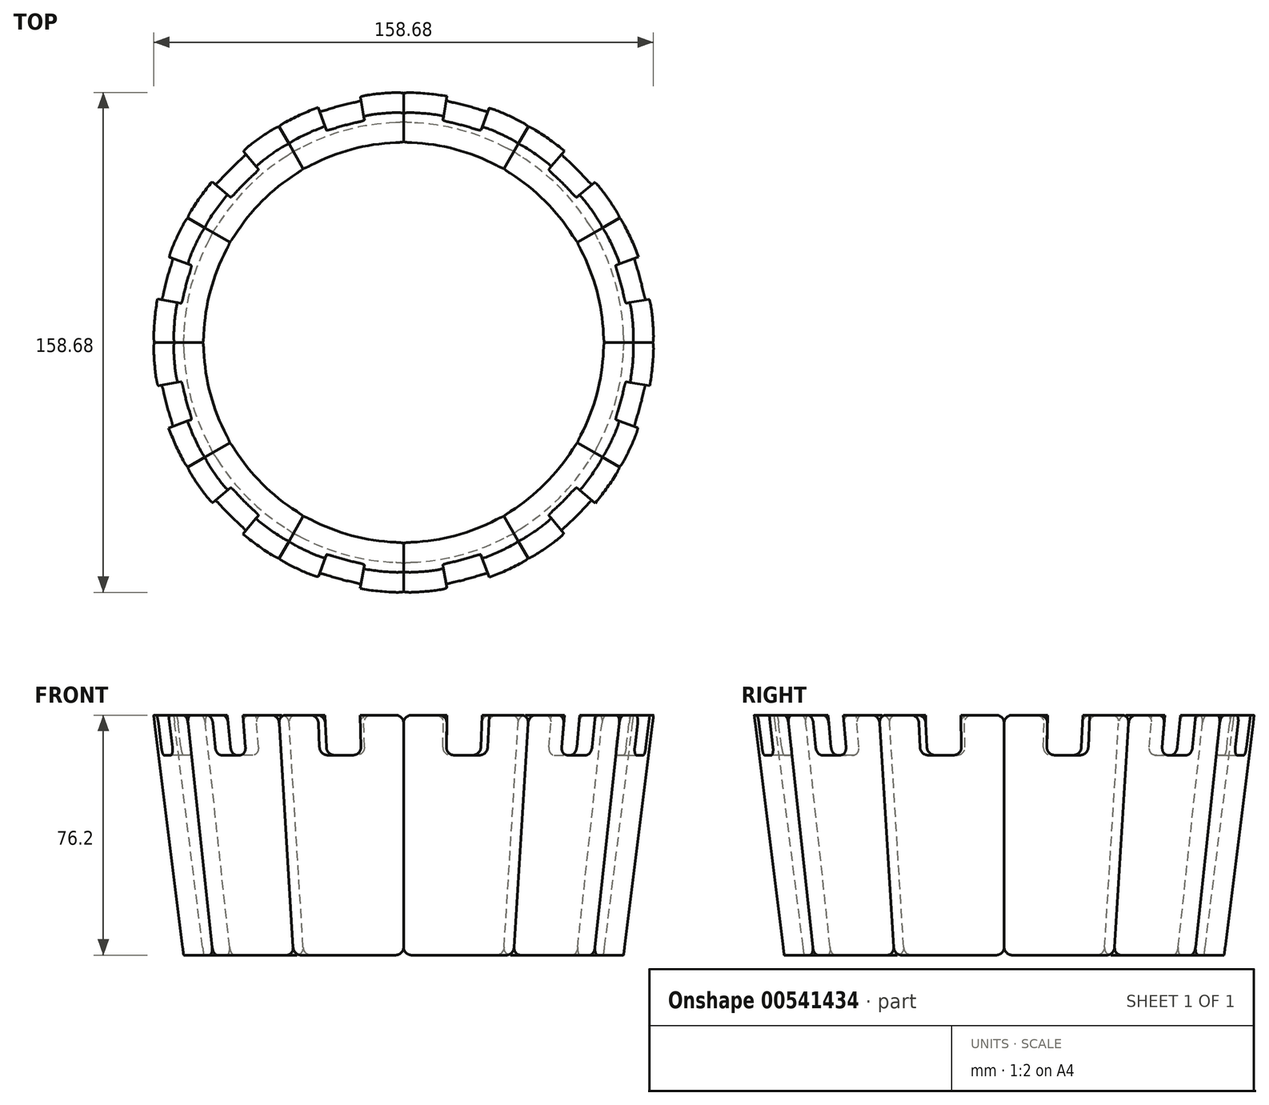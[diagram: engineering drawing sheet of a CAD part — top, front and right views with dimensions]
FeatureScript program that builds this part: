
annotation { "Feature Type Name" : "Feature", "Feature Type Description" : "" }
export const myFeature = defineFeature(function(context is Context, id is Id, definition is map)
    precondition{}
    {
        {
            var Q0;
            Q0=qCreatedBy(makeId("Front.planeOp"),FACE);
            var sketch = newSketch(context, id + "F0", { "sketchPlane" : qUnion([Q0])});
            skLineSegment(sketch, "E0", {"start": v(0, 0) * mm, "end": v(0, 76.2) * mm});
            skLineSegment(sketch, "E1", {"start": v(0, 76.2) * mm, "end": v(79.38, 76.2) * mm});
            skLineSegment(sketch, "E2", {"start": v(0, 0) * mm, "end": v(69.85, 0) * mm});
            skLineSegment(sketch, "E3", {"start": v(69.85, 0) * mm, "end": v(79.38, 76.2) * mm});
            skSolve(sketch);
        }
        {
            var Q0;
            Q0=makeQuery(id+"F0.imprint","IMPRINT",FACE,{"disambiguationData":[TD([[makeQuery(id+"F0.imprint","IMPRINT",EDGE,{"derivedFrom":sQuery(id+"F0.wireOp",EDGE,"E0")}),-1.0]])]});
            var Q1;
            Q1=sQuery(id+"F0.wireOp",EDGE,"E0");
            revolve(context, id + "F1", {"entities" : qUnion([Q0]), "axis" : qUnion([Q1]), "revolveType" : RevolveType.ONE_DIRECTION, "angle" : 30 * degree});
        }
        {
            var Q0;
            Q0=makeQuery(id+"F1.opRevolve","CAP_FACE",FACE,{"disambiguationData":[OSD([sQuery(id+"F0.wireOp",EDGE,"E0"),sQuery(id+"F0.wireOp",EDGE,"E1"),sQuery(id+"F0.wireOp",EDGE,"E2"),sQuery(id+"F0.wireOp",EDGE,"E3")])],"isStart":true});
            var sketch = newSketch(context, id + "F2", { "sketchPlane" : qUnion([Q0])});
            skLineSegment(sketch, "E4", {"start": v(0, 76.2) * mm, "end": v(0, 0) * mm});
            skLineSegment(sketch, "E5", {"start": v(0, 0) * mm, "end": v(69.85, 0) * mm});
            skLineSegment(sketch, "E6", {"start": v(0, 0) * mm, "end": v(63.5, 0) * mm});
            skLineSegment(sketch, "E7", {"start": v(0, 76.2) * mm, "end": v(73.03, 76.2) * mm});
            skLineSegment(sketch, "E8", {"start": v(73.03, 76.2) * mm, "end": v(63.5, 0) * mm});
            skSolve(sketch);
        }
        {
            var Q0;
            Q0=qSketchRegion(id+"F2",true);
            var Q1;
            Q1=sQuery(id+"F2.wireOp",EDGE,"E4");
            revolve(context, id + "F3", {"operationType" : NewBodyOperationType.REMOVE, "entities" : qUnion([Q0]), "axis" : qUnion([Q1]), "revolveType" : RevolveType.FULL, "oppositeDirection" : true});
        }
        {
            var Q0;
            Q0=makeQuery(id+"F1.opRevolve","SWEPT_FACE",FACE,{"disambiguationData":[OSD([sQuery(id+"F0.wireOp",EDGE,"E1")])]});
            var sketch = newSketch(context, id + "F4", { "sketchPlane" : qUnion([Q0])});
            skLineSegment(sketch, "E9", {"start": v(0, 0) * mm, "end": v(68.74, 39.69) * mm, "construction": true});
            skLineSegment(sketch, "E10", {"start": v(0, 0) * mm, "end": v(79.38, 0) * mm, "construction": true});
            skLineSegment(sketch, "E11", {"start": v(0, 0) * mm, "end": v(74.59, 27.15) * mm});
            skLineSegment(sketch, "E12", {"start": v(0, 0) * mm, "end": v(78.17, 13.78) * mm});
            skArc(sketch, "E13", {"start": v(78.17, 13.78) * mm, "mid": v(77.32, 20.72) * mm, "end": v(74.59, 27.15) * mm});
            skSolve(sketch);
        }
        {
            var Q0;
            Q0=qSketchRegion(id+"F4",true);
            extrude(context, id + "F5", {"entities" : qUnion([Q0]), "operationType" : NewBodyOperationType.REMOVE, "oppositeDirection" : true, "depth" : 12.7 * mm, "offsetDistance" : 25.4 * mm});
        }
        {
            var Q0;
            Q0=makeQuery(id+"F1.opRevolve","CAP_EDGE",EDGE,{"disambiguationData":[OSD([sQuery(id+"F0.wireOp",EDGE,"E2")])],"isStart":true});
            var Q1;
            Q1=makeQuery(id+"F1.opRevolve","CAP_EDGE",EDGE,{"disambiguationData":[OSD([sQuery(id+"F0.wireOp",EDGE,"E2")])],"isStart":false});
            var Q2;
            Q2=makeQuery(id+"F5.boolean.opBoolean","COPY",EDGE,{"derivedFrom":makeQuery(id+"F5.opExtrude","CAP_EDGE",EDGE,{"disambiguationData":[OSD([sQuery(id+"F4.wireOp",EDGE,"E11")])],"isStart":true})});
            var Q3;
            Q3=makeQuery(id+"F1.opRevolve","CAP_EDGE",EDGE,{"disambiguationData":[OSD([sQuery(id+"F0.wireOp",EDGE,"E1")])],"isStart":false});
            var Q4;
            Q4=makeQuery(id+"F5.boolean.opBoolean","COPY",EDGE,{"derivedFrom":makeQuery(id+"F5.opExtrude","CAP_EDGE",EDGE,{"disambiguationData":[OSD([sQuery(id+"F4.wireOp",EDGE,"E12")])],"isStart":false})});
            var Q5;
            Q5=makeQuery(id+"F5.boolean.opBoolean","COPY",EDGE,{"derivedFrom":makeQuery(id+"F5.opExtrude","CAP_EDGE",EDGE,{"disambiguationData":[OSD([sQuery(id+"F4.wireOp",EDGE,"E11")])],"isStart":false})});
            var Q6;
            Q6=makeQuery(id+"F1.opRevolve","CAP_EDGE",EDGE,{"disambiguationData":[OSD([sQuery(id+"F0.wireOp",EDGE,"E1")])],"isStart":true});
            var Q7;
            Q7=makeQuery(id+"F5.boolean.opBoolean","COPY",EDGE,{"derivedFrom":makeQuery(id+"F5.opExtrude","CAP_EDGE",EDGE,{"disambiguationData":[OSD([sQuery(id+"F4.wireOp",EDGE,"E12")])],"isStart":true})});
            fillet(context, id + "F6", {"entities" : qUnion([Q0, Q1, Q2, Q3, Q4, Q5, Q6, Q7]), "radius" : 2.54 * mm, "tangentPropagation" : true, "allowEdgeOverflow" : false});
        }
        {
            var Q0;
            Q0=qCreatedBy(makeId("Front.planeOp"),FACE);
            var sketch = newSketch(context, id + "F7", { "sketchPlane" : qUnion([Q0])});
            skLineSegment(sketch, "E14", {"start": v(0, 0) * mm, "end": v(0, 56.18) * mm, "construction": true});
            skSolve(sketch);
        }
        {
            var Q0;
            Q0=makeQuery(id+"F1.opRevolve","SWEPT_BODY",BODY,{"disambiguationData":[OSD([sQuery(id+"F0.wireOp",EDGE,"E0"),sQuery(id+"F0.wireOp",EDGE,"E1"),sQuery(id+"F0.wireOp",EDGE,"E2"),sQuery(id+"F0.wireOp",EDGE,"E3")])]});
            var Q1;
            Q1=sQuery(id+"F7.wireOp",EDGE,"E14");
            circularPattern(context, id + "F8", {"entities" : qUnion([Q0]), "axis" : qUnion([Q1]), "angle" : 360 * degree, "instanceCount" : 12, "equalSpace" : true});
        }
    });
